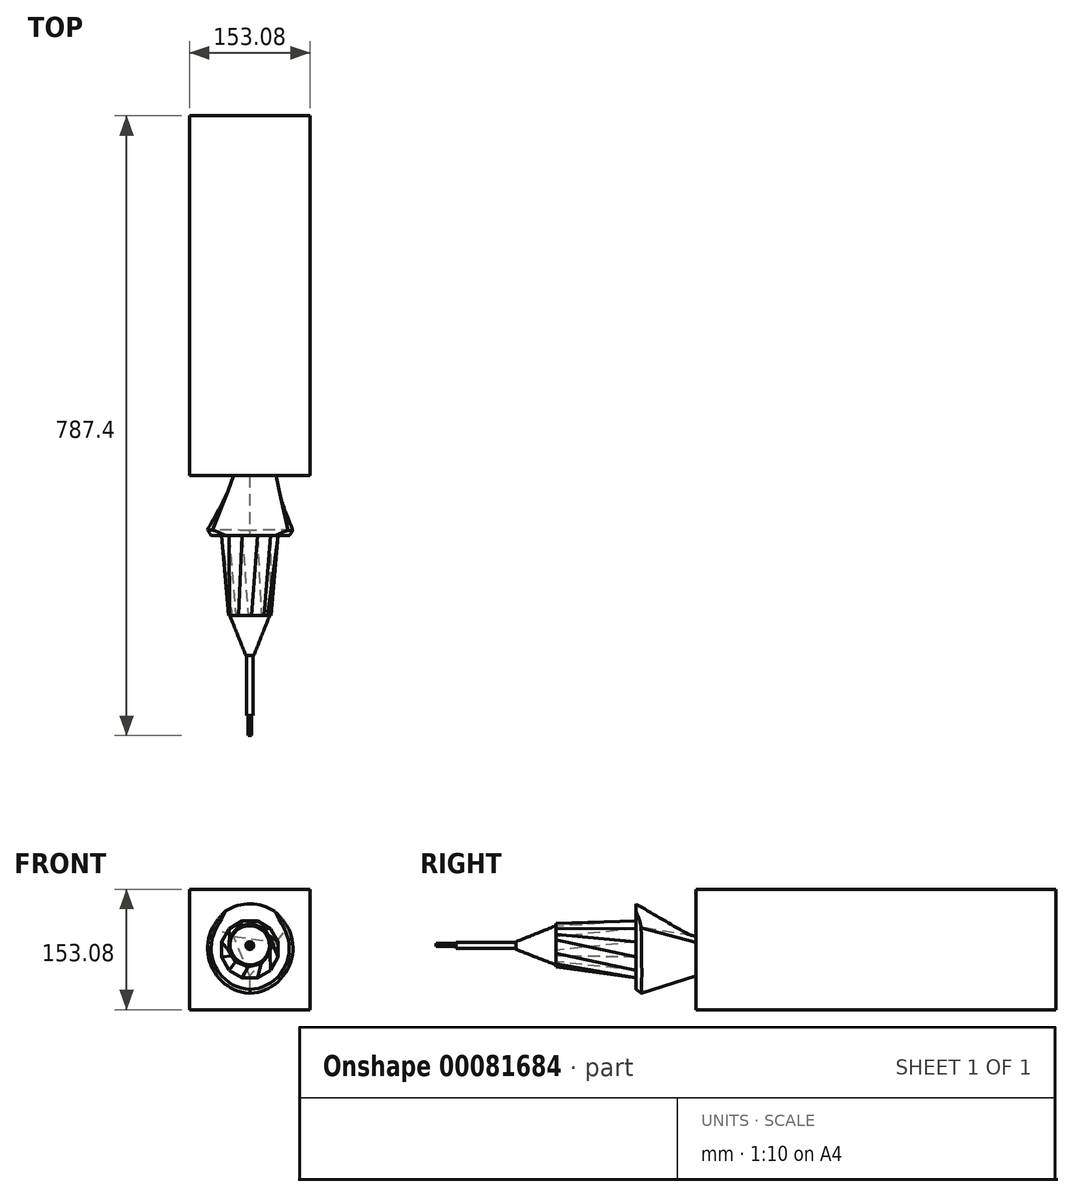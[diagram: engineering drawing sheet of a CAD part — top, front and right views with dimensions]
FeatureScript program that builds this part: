
annotation { "Feature Type Name" : "Feature", "Feature Type Description" : "" }
export const myFeature = defineFeature(function(context is Context, id is Id, definition is map)
    precondition{}
    {
        {
            var Q0;
            Q0=qCreatedBy(makeId("Front.planeOp"),FACE);
            var sketch = newSketch(context, id + "F0", { "sketchPlane" : qUnion([Q0])});
            skCircle(sketch, "E0", {"center": v(0, 0) * mm, "radius": 57.79 * mm});
            skSolve(sketch);
        }
        {
            var Q0;
            Q0=qCreatedBy(makeId("Front.planeOp"),FACE);
            cPlane(context, id + "F1", {"entities" : qUnion([Q0]), "cplaneType" : CPlaneType.OFFSET, "offset" : 76.2 * mm, "oppositeDirection" : true, "width" : 152.4 * mm, "height" : 152.4 * mm});
        }
        {
            var Q0;
            Q0=qCreatedBy(id+"F1.planeOp",FACE);
            var sketch = newSketch(context, id + "F2", { "sketchPlane" : qUnion([Q0])});
            skPoint(sketch, "E1.middle", {"position": v(0, 0) * mm});
            skLineSegment(sketch, "E2", {"start": v(0, -33.69) * mm, "end": v(-20.46, 16.72) * mm});
            skLineSegment(sketch, "E3", {"start": v(-20.46, 16.72) * mm, "end": v(33.43, 9.24) * mm});
            skLineSegment(sketch, "E4", {"start": v(33.43, 9.24) * mm, "end": v(0, -33.69) * mm});
            skSolve(sketch);
        }
        {
            var Q0;
            Q0=makeQuery(id+"F2.imprint","IMPRINT",FACE,{"disambiguationData":[TD([[makeQuery(id+"F2.imprint","IMPRINT",EDGE,{"derivedFrom":sQuery(id+"F2.wireOp",EDGE,"E2")}),-1.0]])]});
            var Q1;
            Q1=makeQuery(id+"F0.imprint","IMPRINT",FACE,{"disambiguationData":[TD([[makeQuery(id+"F0.imprint","IMPRINT",EDGE,{"derivedFrom":sQuery(id+"F0.wireOp",EDGE,"E0")}),1.0]])]});
            loft(context, id + "F3", {"sheetProfilesArray" : [{ "sheetProfileEntities" : qUnion([Q0]) }, { "sheetProfileEntities" : qUnion([Q1]) }]});
        }
        {
            var Q0;
            Q0=qCreatedBy(makeId("Front.planeOp"),FACE);
            var sketch = newSketch(context, id + "F4", { "sketchPlane" : qUnion([Q0])});
            skCircle(sketch, "E5.cCircle", {"center": v(0, 0) * mm, "radius": 35.98 * mm, "construction": true});
            skLineSegment(sketch, "E5.0", {"start": v(-9.64, 35.98) * mm, "end": v(9.64, 35.98) * mm});
            skLineSegment(sketch, "E5.1", {"start": v(9.64, 35.98) * mm, "end": v(26.34, 26.34) * mm});
            skLineSegment(sketch, "E5.2", {"start": v(26.34, 26.34) * mm, "end": v(35.98, 9.64) * mm});
            skLineSegment(sketch, "E5.3", {"start": v(35.98, 9.64) * mm, "end": v(35.98, -9.64) * mm});
            skLineSegment(sketch, "E5.4", {"start": v(35.98, -9.64) * mm, "end": v(26.34, -26.34) * mm});
            skLineSegment(sketch, "E5.5", {"start": v(26.34, -26.34) * mm, "end": v(9.64, -35.98) * mm});
            skLineSegment(sketch, "E5.6", {"start": v(9.64, -35.98) * mm, "end": v(-9.64, -35.98) * mm});
            skLineSegment(sketch, "E5.7", {"start": v(-9.64, -35.98) * mm, "end": v(-26.34, -26.34) * mm});
            skLineSegment(sketch, "E5.8", {"start": v(-26.34, -26.34) * mm, "end": v(-35.98, -9.64) * mm});
            skLineSegment(sketch, "E5.9", {"start": v(-35.98, -9.64) * mm, "end": v(-35.98, 9.64) * mm});
            skLineSegment(sketch, "E5.10", {"start": v(-35.98, 9.64) * mm, "end": v(-26.34, 26.34) * mm});
            skLineSegment(sketch, "E5.11", {"start": v(-26.34, 26.34) * mm, "end": v(-9.64, 35.98) * mm});
            skPoint(sketch, "E5.0.midPoint", {"position": v(0, 35.98) * mm});
            skSolve(sketch);
        }
        {
            var Q0;
            Q0=qCreatedBy(makeId("Front.planeOp"),FACE);
            cPlane(context, id + "F5", {"entities" : qUnion([Q0]), "cplaneType" : CPlaneType.OFFSET, "offset" : 101.6 * mm, "width" : 152.4 * mm, "height" : 152.4 * mm});
        }
        {
            var Q0;
            Q0=qCreatedBy(id+"F5.planeOp",FACE);
            var sketch = newSketch(context, id + "F6", { "sketchPlane" : qUnion([Q0])});
            skPoint(sketch, "E6.0.midPoint", {"position": v(-0.75, 20.14) * mm});
            skPoint(sketch, "E7.0.midPoint", {"position": v(14.27, -14.13) * mm});
            skPoint(sketch, "E8.0.midPoint", {"position": v(22.66, -4.68) * mm});
            skCircle(sketch, "E9.cCircle", {"center": v(0, 5.45) * mm, "radius": 26.43 * mm, "construction": true});
            skLineSegment(sketch, "E9.0", {"start": v(2.1, 33.16) * mm, "end": v(17.98, 26.64) * mm});
            skLineSegment(sketch, "E9.1", {"start": v(17.98, 26.64) * mm, "end": v(27, 12.02) * mm});
            skLineSegment(sketch, "E9.2", {"start": v(27, 12.02) * mm, "end": v(25.7, -5.1) * mm});
            skLineSegment(sketch, "E9.3", {"start": v(25.7, -5.1) * mm, "end": v(14.6, -18.2) * mm});
            skLineSegment(sketch, "E9.4", {"start": v(14.6, -18.2) * mm, "end": v(-2.1, -22.27) * mm});
            skLineSegment(sketch, "E9.5", {"start": v(-2.1, -22.27) * mm, "end": v(-17.98, -15.74) * mm});
            skLineSegment(sketch, "E9.6", {"start": v(-17.98, -15.74) * mm, "end": v(-27, -1.13) * mm});
            skLineSegment(sketch, "E9.7", {"start": v(-27, -1.13) * mm, "end": v(-25.7, 16) * mm});
            skLineSegment(sketch, "E9.8", {"start": v(-25.7, 16) * mm, "end": v(-14.6, 29.1) * mm});
            skLineSegment(sketch, "E9.9", {"start": v(-14.6, 29.1) * mm, "end": v(2.1, 33.16) * mm});
            skPoint(sketch, "E9.0.midPoint", {"position": v(10.04, 29.9) * mm});
            skSolve(sketch);
        }
        {
            var Q1;
            Q1=makeQuery(id+"F4.imprint","IMPRINT",FACE,{"disambiguationData":[TD([[makeQuery(id+"F4.imprint","IMPRINT",EDGE,{"derivedFrom":sQuery(id+"F4.wireOp",EDGE,"E5.0")}),-1.0]])]});
            var Q2;
            Q2=makeQuery(id+"F6.imprint","IMPRINT",FACE,{"disambiguationData":[TD([[makeQuery(id+"F6.imprint","IMPRINT",EDGE,{"derivedFrom":sQuery(id+"F6.wireOp",EDGE,"E9.0")}),-1.0]])]});
            loft(context, id + "F7", {"operationType" : NewBodyOperationType.ADD, "sheetProfilesArray" : [{ "sheetProfileEntities" : qUnion([Q1]) }, { "sheetProfileEntities" : qUnion([Q2]) }]});
        }
        {
            var Q0;
            Q0=qCreatedBy(id+"F5.planeOp",FACE);
            cPlane(context, id + "F8", {"entities" : qUnion([Q0]), "cplaneType" : CPlaneType.OFFSET, "offset" : 50.8 * mm, "width" : 152.4 * mm, "height" : 152.4 * mm});
        }
        {
            var Q0;
            Q0=makeQuery(id+"F7.opLoft","CAP_FACE",FACE,{"disambiguationData":[OSD([makeQuery(id+"F6.imprint","IMPRINT",FACE,{"disambiguationData":[TD([[makeQuery(id+"F6.imprint","IMPRINT",EDGE,{"derivedFrom":sQuery(id+"F6.wireOp",EDGE,"E9.0")}),-1.0]])]})])],"isStart":true});
            var sketch = newSketch(context, id + "F9", { "sketchPlane" : qUnion([Q0])});
            skEllipse(sketch, "E10", {"center": v(0, 5.28) * mm, "majorRadius": 24.86 * mm, "minorRadius": 25.3 * mm, "majorAxis": v(0.37, 0.93)});
            skSolve(sketch);
        }
        {
            var Q0;
            Q0=qCreatedBy(id+"F8.planeOp",FACE);
            var sketch = newSketch(context, id + "F10", { "sketchPlane" : qUnion([Q0])});
            skCircle(sketch, "E11", {"center": v(0, 4.85) * mm, "radius": 4.85 * mm});
            skSolve(sketch);
        }
        {
            var Q1;
            Q1=makeQuery(id+"F9.imprint","IMPRINT",FACE,{"disambiguationData":[TD([[makeQuery(id+"F9.imprint","IMPRINT",EDGE,{"derivedFrom":sQuery(id+"F9.wireOp",EDGE,"E10")}),1.0]])]});
            var Q2;
            Q2=makeQuery(id+"F10.imprint","IMPRINT",FACE,{"disambiguationData":[TD([[makeQuery(id+"F10.imprint","IMPRINT",EDGE,{"derivedFrom":sQuery(id+"F10.wireOp",EDGE,"E11")}),1.0]])]});
            loft(context, id + "F11", {"operationType" : NewBodyOperationType.ADD, "sheetProfilesArray" : [{ "sheetProfileEntities" : qUnion([Q1]) }, { "sheetProfileEntities" : qUnion([Q2]) }]});
        }
        {
            var Q0;
            Q0=qCreatedBy(id+"F8.planeOp",FACE);
            var sketch = newSketch(context, id + "F12", { "sketchPlane" : qUnion([Q0])});
            skLineSegment(sketch, "E12.bottom", {"start": v(4.09, 9.14) * mm, "end": v(-4.09, 9.14) * mm});
            skLineSegment(sketch, "E12.top", {"start": v(4.09, 1.36) * mm, "end": v(-4.09, 1.36) * mm});
            skLineSegment(sketch, "E12.left", {"start": v(4.09, 9.14) * mm, "end": v(4.09, 1.36) * mm});
            skLineSegment(sketch, "E12.right", {"start": v(-4.09, 9.14) * mm, "end": v(-4.09, 1.36) * mm});
            skPoint(sketch, "E12.middle", {"position": v(0, 5.25) * mm});
            skSolve(sketch);
        }
        {
            var Q0;
            Q0=qCreatedBy(id+"F8.planeOp",FACE);
            cPlane(context, id + "F13", {"entities" : qUnion([Q0]), "cplaneType" : CPlaneType.OFFSET, "offset" : 76.2 * mm, "width" : 152.4 * mm, "height" : 152.4 * mm});
        }
        {
            var Q0;
            Q0=qCreatedBy(id+"F13.planeOp",FACE);
            var sketch = newSketch(context, id + "F14", { "sketchPlane" : qUnion([Q0])});
            skCircle(sketch, "E13", {"center": v(0, 5.64) * mm, "radius": 2.03 * mm});
            skSolve(sketch);
        }
        {
            var Q0;
            Q0=makeQuery(id+"F12.imprint","IMPRINT",FACE,{"disambiguationData":[TD([[makeQuery(id+"F12.imprint","IMPRINT",EDGE,{"derivedFrom":sQuery(id+"F12.wireOp",EDGE,"E12.bottom")}),1.0]])]});
            extrude(context, id + "F15", {"entities" : qUnion([Q0]), "operationType" : NewBodyOperationType.ADD, "depth" : 76.2 * mm});
        }
        {
            var Q0;
            Q0=makeQuery(id+"F14.imprint","IMPRINT",FACE,{"disambiguationData":[TD([[makeQuery(id+"F14.imprint","IMPRINT",EDGE,{"derivedFrom":sQuery(id+"F14.wireOp",EDGE,"E13")}),1.0]])]});
            extrude(context, id + "F16", {"entities" : qUnion([Q0]), "operationType" : NewBodyOperationType.ADD, "depth" : 25.4 * mm});
        }
        {
            var Q0;
            Q0=makeQuery(id+"F3.opLoft","MID_CAP_EDGE",EDGE,{"disambiguationData":[OSD([sQuery(id+"F0.wireOp",EDGE,"E0"),sQuery(id+"F2.wireOp",EDGE,"E2"),sQuery(id+"F2.wireOp",EDGE,"E3"),sQuery(id+"F2.wireOp",EDGE,"E4")]),OD(0.0)],"capPos":1.0});
            var Q1;
            Q1=makeQuery(id+"F3.opLoft","MID_CAP_EDGE",EDGE,{"disambiguationData":[OSD([sQuery(id+"F0.wireOp",EDGE,"E0"),sQuery(id+"F2.wireOp",EDGE,"E2"),sQuery(id+"F2.wireOp",EDGE,"E4")])],"capPos":1.0});
            var Q2;
            Q2=makeQuery(id+"F3.opLoft","MID_CAP_EDGE",EDGE,{"disambiguationData":[OSD([sQuery(id+"F0.wireOp",EDGE,"E0"),sQuery(id+"F2.wireOp",EDGE,"E2"),sQuery(id+"F2.wireOp",EDGE,"E3"),sQuery(id+"F2.wireOp",EDGE,"E4")]),OD(1.0)],"capPos":1.0});
            chamfer(context, id + "F17", {"entities" : qUnion([Q0, Q1, Q2]), "width" : 5.08 * mm, "tangentPropagation" : true});
        }
        {
            var Q0;
            Q0=qCreatedBy(id+"F1.planeOp",FACE);
            var sketch = newSketch(context, id + "F18", { "sketchPlane" : qUnion([Q0])});
            skLineSegment(sketch, "E14.bottom", {"start": v(-76.54, 76.54) * mm, "end": v(76.54, 76.54) * mm});
            skLineSegment(sketch, "E14.top", {"start": v(-76.54, -76.54) * mm, "end": v(76.54, -76.54) * mm});
            skLineSegment(sketch, "E14.left", {"start": v(-76.54, 76.54) * mm, "end": v(-76.54, -76.54) * mm});
            skLineSegment(sketch, "E14.right", {"start": v(76.54, 76.54) * mm, "end": v(76.54, -76.54) * mm});
            skPoint(sketch, "E14.middle", {"position": v(0, 0) * mm});
            skSolve(sketch);
        }
        {
            var Q0;
            Q0 = qSketchRegion(id + "F18", true);
            extrude(context, id + "F19", {"entities" : qUnion([Q0]), "operationType" : NewBodyOperationType.ADD, "oppositeDirection" : true, "depth" : 457.2 * mm});
        }
    });
